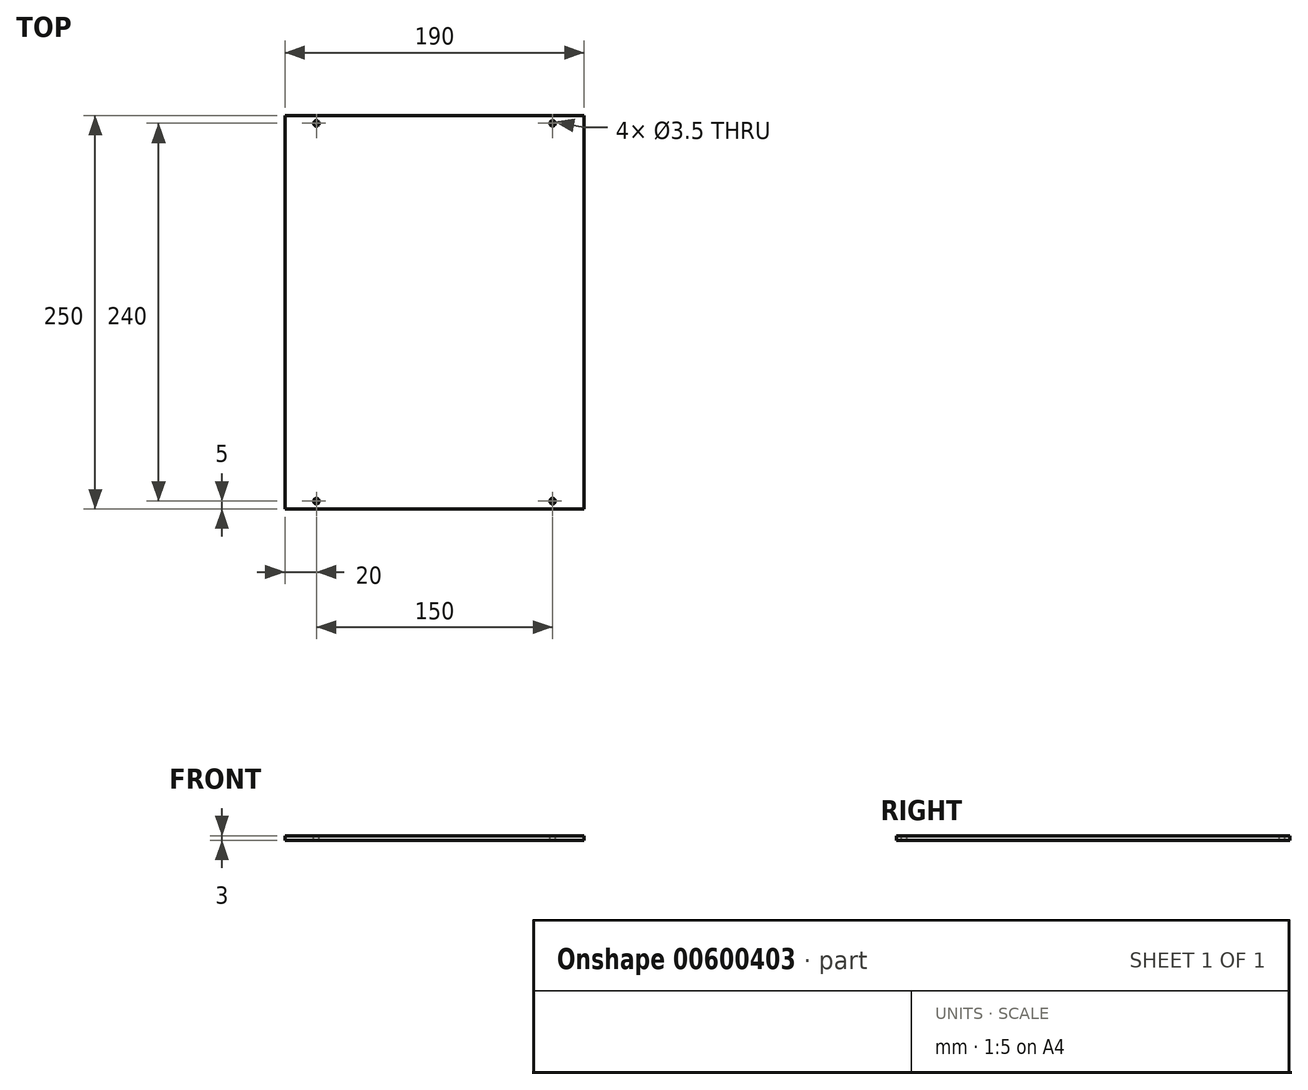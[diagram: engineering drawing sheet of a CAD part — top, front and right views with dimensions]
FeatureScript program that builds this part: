
annotation { "Feature Type Name" : "Feature", "Feature Type Description" : "" }
export const myFeature = defineFeature(function(context is Context, id is Id, definition is map)
    precondition{}
    {
        {
            var Q0;
            Q0=qCreatedBy(makeId("Top.planeOp"),FACE);
            var sketch = newSketch(context, id + "F0", { "sketchPlane" : qUnion([Q0])});
            skLineSegment(sketch, "E0.bottom", {"start": v(95, 125) * mm, "end": v(-95, 125) * mm});
            skLineSegment(sketch, "E0.top", {"start": v(95, -125) * mm, "end": v(-95, -125) * mm});
            skLineSegment(sketch, "E0.left", {"start": v(95, 125) * mm, "end": v(95, -125) * mm});
            skLineSegment(sketch, "E0.right", {"start": v(-95, 125) * mm, "end": v(-95, -125) * mm});
            skPoint(sketch, "E0.middle", {"position": v(0, 0) * mm});
            skCircle(sketch, "E1", {"center": v(-75, 120) * mm, "radius": 1.75 * mm});
            skCircle(sketch, "E2", {"center": v(75, 120) * mm, "radius": 1.75 * mm});
            skCircle(sketch, "E3", {"center": v(-75, -120) * mm, "radius": 1.75 * mm});
            skCircle(sketch, "E4", {"center": v(75, -120) * mm, "radius": 1.75 * mm});
            skSolve(sketch);
        }
        {
            var Q0;
            Q0=qSketchRegion(id+"F0",true);
            extrude(context, id + "F1", {"entities" : qUnion([Q0]), "oppositeDirection" : true, "depth" : 3 * mm});
        }
    });
